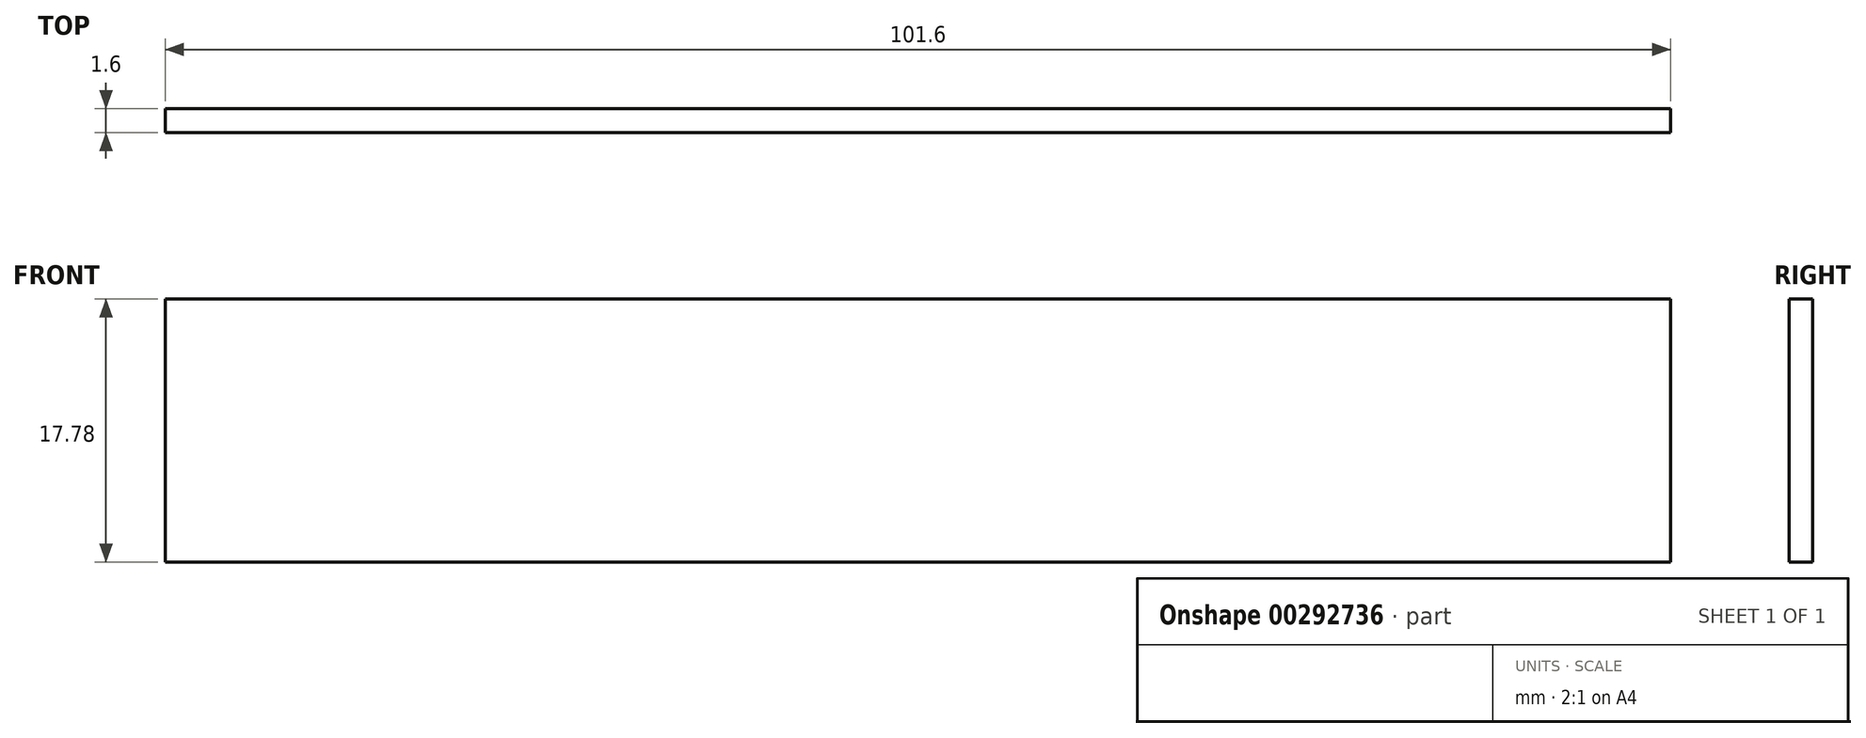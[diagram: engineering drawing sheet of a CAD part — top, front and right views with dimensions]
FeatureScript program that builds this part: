
annotation { "Feature Type Name" : "Feature", "Feature Type Description" : "" }
export const myFeature = defineFeature(function(context is Context, id is Id, definition is map)
    precondition{}
    {
        {
            var Q0;
            Q0=qCreatedBy(makeId("Front.planeOp"),FACE);
            var sketch = newSketch(context, id + "F0", { "sketchPlane" : qUnion([Q0])});
            skLineSegment(sketch, "E0.bottom", {"start": v(50.8, 8.9) * mm, "end": v(-50.8, 8.9) * mm});
            skLineSegment(sketch, "E0.top", {"start": v(50.8, -8.9) * mm, "end": v(-50.8, -8.9) * mm});
            skLineSegment(sketch, "E0.left", {"start": v(50.8, 8.9) * mm, "end": v(50.8, -8.9) * mm});
            skLineSegment(sketch, "E0.right", {"start": v(-50.8, 8.9) * mm, "end": v(-50.8, -8.9) * mm});
            skPoint(sketch, "E0.middle", {"position": v(0, 0) * mm});
            skSolve(sketch);
        }
        {
            var Q0;
            Q0=makeQuery(id+"F0.imprint","IMPRINT",FACE,{"disambiguationData":[TD([[makeQuery(id+"F0.imprint","IMPRINT",EDGE,{"derivedFrom":sQuery(id+"F0.wireOp",EDGE,"E0.bottom")}),1.0]])]});
            extrude(context, id + "F1", {"entities" : qUnion([Q0]), "depth" : 1.6 * mm, "offsetDistance" : 25.4 * mm});
        }
    });
